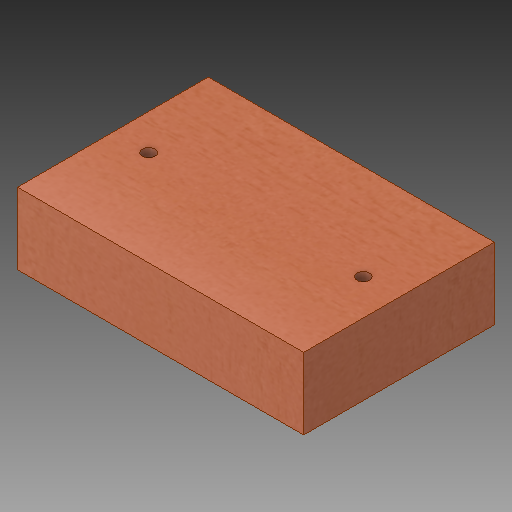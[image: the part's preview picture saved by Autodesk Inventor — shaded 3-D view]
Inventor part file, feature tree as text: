
AUTODESK INVENTOR PART (.ipt)
format: ipt  version: 2019.3 (Build 233278000, 278)  size: 202,752 bytes
history: native  units: in
note: dims shown in document units (in); Inventor stores cm internally (conversion verified against a paired STEP export)
features: hole x2, sketch x2, extrude x1
ambient origin geometry x8: Origin, YZ Plane, XZ Plane, XY Plane, X Axis, Y Axis, Z Axis, Center Point
bodies: Solid1 (feature_tree)
feature tree (5):
  extrude  "Extrusion1"  Depth=4.0in
  hole  "Hole2"  [1 undecoded]
  sketch  "Sketch1"  dims[d0=6.0in d1=4.0in]
  sketch  "Sketch2"  dims[d2=1.5in d3=0.0in d4=0.266in d5=0.75in d6=0.375in d7=0.25in d8=0.5635in d9=1.0in d10=0.0in]
  hole  "Hole1"  [1 undecoded]
note: 2 required parameter values undecoded (feature->parameter linkage not recoverable at this tier; creation-order binding heuristic only, values carry confidence <= 0.55)
